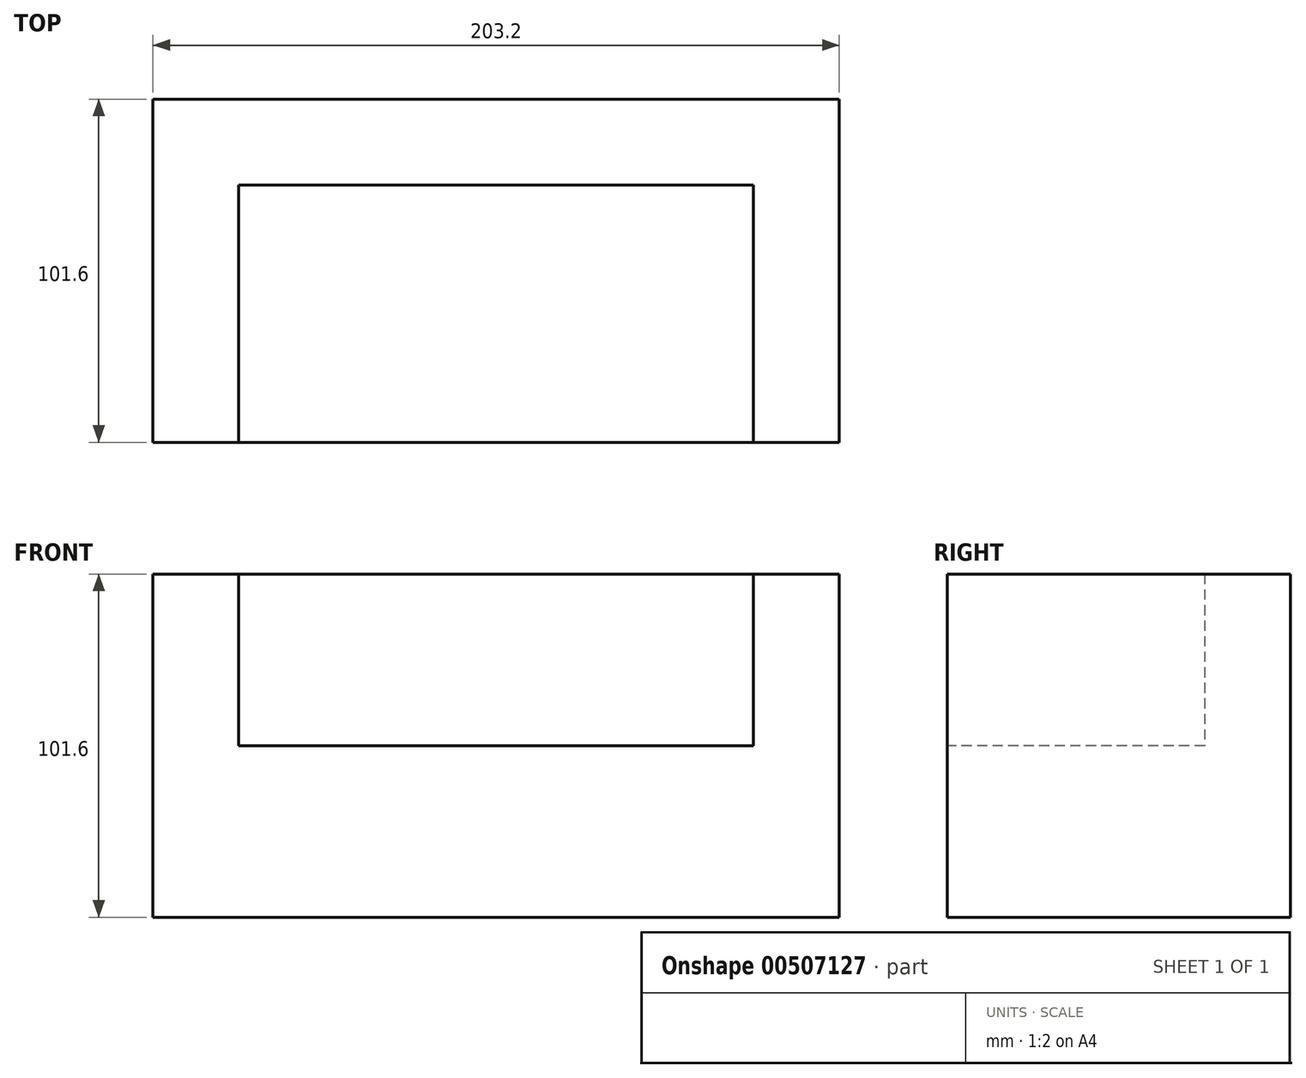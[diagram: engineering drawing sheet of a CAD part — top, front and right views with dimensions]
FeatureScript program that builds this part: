
annotation { "Feature Type Name" : "Feature", "Feature Type Description" : "" }
export const myFeature = defineFeature(function(context is Context, id is Id, definition is map)
    precondition{}
    {
        {
            var Q0;
            Q0=qCreatedBy(makeId("Front.planeOp"),FACE);
            var sketch = newSketch(context, id + "F0", { "sketchPlane" : qUnion([Q0])});
            skLineSegment(sketch, "E0.bottom", {"start": v(-99.29, 20.53) * mm, "end": v(103.91, 20.53) * mm});
            skLineSegment(sketch, "E0.top", {"start": v(-99.29, -81.07) * mm, "end": v(103.91, -81.07) * mm});
            skLineSegment(sketch, "E0.left", {"start": v(-99.29, 20.53) * mm, "end": v(-99.29, -81.07) * mm});
            skLineSegment(sketch, "E0.right", {"start": v(103.91, 20.53) * mm, "end": v(103.91, -81.07) * mm});
            skLineSegment(sketch, "E1.bottom", {"start": v(-56.08, 20.53) * mm, "end": v(62.2, 20.53) * mm});
            skLineSegment(sketch, "E1.top", {"start": v(-56.08, -31) * mm, "end": v(62.2, -31) * mm});
            skLineSegment(sketch, "E1.left", {"start": v(-56.08, 20.53) * mm, "end": v(-56.08, -31) * mm});
            skLineSegment(sketch, "E1.right", {"start": v(62.2, 20.53) * mm, "end": v(62.2, -31) * mm});
            skSolve(sketch);
        }
        {
            var Q0;
            Q0 = qSketchRegion(id + "F0", true);
            extrude(context, id + "F1", {"entities" : qUnion([Q0]), "oppositeDirection" : true, "depth" : 101.6 * mm});
        }
        {
            var Q0;
            Q0=qCreatedBy(makeId("Front.planeOp"),FACE);
            var sketch = newSketch(context, id + "F2", { "sketchPlane" : qUnion([Q0])});
            skLineSegment(sketch, "E2.bottom", {"start": v(78.51, 20.53) * mm, "end": v(-73.89, 20.53) * mm});
            skLineSegment(sketch, "E2.top", {"start": v(78.51, -30.27) * mm, "end": v(-73.89, -30.27) * mm});
            skLineSegment(sketch, "E2.left", {"start": v(78.51, 20.53) * mm, "end": v(78.51, -30.27) * mm});
            skLineSegment(sketch, "E2.right", {"start": v(-73.89, 20.53) * mm, "end": v(-73.89, -30.27) * mm});
            skSolve(sketch);
        }
        {
            var Q0;
            Q0 = qSketchRegion(id + "F2", true);
            extrude(context, id + "F3", {"entities" : qUnion([Q0]), "operationType" : NewBodyOperationType.REMOVE, "oppositeDirection" : true, "depth" : 76.2 * mm});
        }
    });
